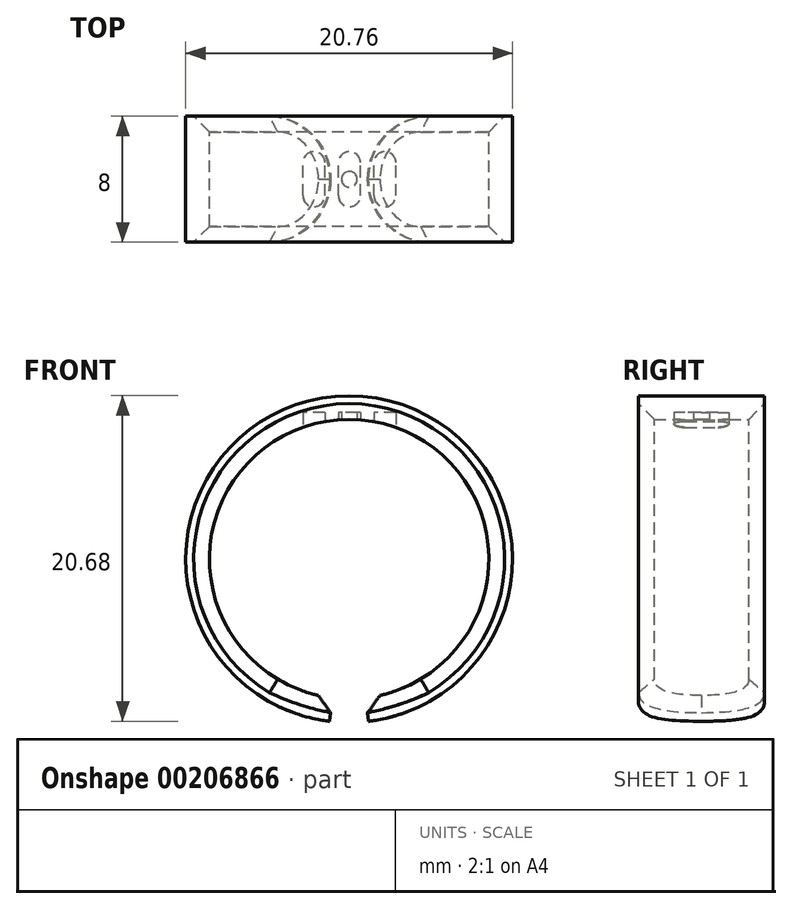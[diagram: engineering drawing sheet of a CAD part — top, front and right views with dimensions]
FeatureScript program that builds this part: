
annotation { "Feature Type Name" : "Feature", "Feature Type Description" : "" }
export const myFeature = defineFeature(function(context is Context, id is Id, definition is map)
    precondition{}
    {
        {
            var Q0;
            Q0=qCreatedBy(makeId("Front.planeOp"),FACE);
            var sketch = newSketch(context, id + "F0", { "sketchPlane" : qUnion([Q0])});
            skCircle(sketch, "E0", {"center": v(0, 0) * mm, "radius": 8.88 * mm});
            skCircle(sketch, "E1.0", {"center": v(0, 0) * mm, "radius": 10.38 * mm});
            skLineSegment(sketch, "E2", {"start": v(0, 0) * mm, "end": v(-1.24, -10.3) * mm});
            skLineSegment(sketch, "E3.MirrorCS", {"start": v(0, 0) * mm, "end": v(1.24, -10.3) * mm});
            skSolve(sketch);
        }
        {
            var Q0;
            {var subQ0=sQuery(id+"F0.wireOp",EDGE,"E2");var subQ1=sQuery(id+"F0.wireOp",EDGE,"E0");var subQ2=makeQuery(id+"F0.imprint","INTERSECT",VERTEX,{"derivedFrom":[subQ1,subQ0]});Q0=makeQuery(id+"F0.imprint","IMPRINT",FACE,{"disambiguationData":[TD([[makeQuery(id+"F0.imprint","IMPRINT",EDGE,{"disambiguationData":[TD([[subQ2,1.0]])],"derivedFrom":subQ1}),-1.0]])]});}
            extrude(context, id + "F1", {"entities" : qUnion([Q0]), "depth" : 4 * mm, "hasSecondDirection" : true, "secondDirectionOppositeDirection" : true, "secondDirectionDepth" : 4 * mm});
        }
        {
            var Q0;
            Q0=makeQuery(id+"F1.opExtrude","CAP_EDGE",EDGE,{"disambiguationData":[OSD([sQuery(id+"F0.wireOp",EDGE,"E3.MirrorCS")])],"isStart":false});
            var Q1;
            Q1=makeQuery(id+"F1.opExtrude","CAP_EDGE",EDGE,{"disambiguationData":[OSD([sQuery(id+"F0.wireOp",EDGE,"E2")])],"isStart":false});
            var Q2;
            Q2=makeQuery(id+"F1.opExtrude","CAP_EDGE",EDGE,{"disambiguationData":[OSD([sQuery(id+"F0.wireOp",EDGE,"E2")])],"isStart":true});
            var Q3;
            Q3=makeQuery(id+"F1.opExtrude","CAP_EDGE",EDGE,{"disambiguationData":[OSD([sQuery(id+"F0.wireOp",EDGE,"E3.MirrorCS")])],"isStart":true});
            fillet(context, id + "F2", {"entities" : qUnion([Q0, Q1, Q2, Q3]), "radius" : 4 * mm, "tangentPropagation" : true, "allowEdgeOverflow" : false});
        }
        {
            var Q0;
            Q0=makeQuery(id+"F1.opExtrude","CAP_EDGE",EDGE,{"disambiguationData":[OSD([sQuery(id+"F0.wireOp",EDGE,"E0")])],"isStart":true});
            var Q1;
            Q1=makeQuery(id+"F1.opExtrude","CAP_EDGE",EDGE,{"disambiguationData":[OSD([sQuery(id+"F0.wireOp",EDGE,"E0")])],"isStart":false});
            var Q2;
            Q2=makeQuery(id+"F2.opFillet","BLEND_EDGE",EDGE,{"blendedFrom":[makeQuery(id+"F1.opExtrude","CAP_EDGE",EDGE,{"disambiguationData":[OSD([sQuery(id+"F0.wireOp",EDGE,"E2")])],"isStart":false}),makeQuery(id+"F1.opExtrude","SWEPT_FACE",FACE,{"disambiguationData":[OSD([sQuery(id+"F0.wireOp",EDGE,"E0")])]})],"blendedInto":[makeQuery(id+"F1.opExtrude","SWEPT_FACE",FACE,{"disambiguationData":[OSD([sQuery(id+"F0.wireOp",EDGE,"E0")])]})]});
            var Q3;
            Q3=makeQuery(id+"F2.opFillet","BLEND_EDGE",EDGE,{"blendedFrom":[makeQuery(id+"F1.opExtrude","CAP_EDGE",EDGE,{"disambiguationData":[OSD([sQuery(id+"F0.wireOp",EDGE,"E3.MirrorCS")])],"isStart":true}),makeQuery(id+"F1.opExtrude","SWEPT_FACE",FACE,{"disambiguationData":[OSD([sQuery(id+"F0.wireOp",EDGE,"E0")])]})],"blendedInto":[makeQuery(id+"F1.opExtrude","SWEPT_FACE",FACE,{"disambiguationData":[OSD([sQuery(id+"F0.wireOp",EDGE,"E0")])]})]});
            chamfer(context, id + "F3", {"entities" : qUnion([Q0, Q1, Q2, Q3]), "width" : 1 * mm, "tangentPropagation" : true});
        }
        {
            var Q0;
            Q0=qCreatedBy(makeId("Top.planeOp"),FACE);
            var sketch = newSketch(context, id + "F4", { "sketchPlane" : qUnion([Q0])});
            skLineSegment(sketch, "E4.bottom", {"start": v(-0.68, 1.05) * mm, "end": v(-0.68, -1.05) * mm});
            skArc(sketch, "E5.filletArc", {"start": v(0.72, 1.05) * mm, "mid": v(0.51, 1.54) * mm, "end": v(0.02, 1.75) * mm});
            skArc(sketch, "E6.filletArc", {"start": v(0.02, 1.75) * mm, "mid": v(-0.48, 1.54) * mm, "end": v(-0.68, 1.05) * mm});
            skArc(sketch, "E7.filletArc", {"start": v(0.02, -1.75) * mm, "mid": v(0.51, -1.54) * mm, "end": v(0.72, -1.05) * mm});
            skArc(sketch, "E8.filletArc", {"start": v(-0.68, -1.05) * mm, "mid": v(-0.48, -1.54) * mm, "end": v(0.02, -1.75) * mm});
            skLineSegment(sketch, "E9.bottom", {"start": v(-2.94, 1.05) * mm, "end": v(-2.94, -1.05) * mm});
            skLineSegment(sketch, "E9.top", {"start": v(-1.54, 1.05) * mm, "end": v(-1.54, -1.05) * mm});
            skArc(sketch, "E10.filletArc", {"start": v(-1.54, 1.05) * mm, "mid": v(-1.74, 1.54) * mm, "end": v(-2.24, 1.75) * mm});
            skArc(sketch, "E11.filletArc", {"start": v(-2.24, 1.75) * mm, "mid": v(-2.73, 1.54) * mm, "end": v(-2.94, 1.05) * mm});
            skArc(sketch, "E12.filletArc", {"start": v(-2.24, -1.75) * mm, "mid": v(-1.74, -1.54) * mm, "end": v(-1.54, -1.05) * mm});
            skArc(sketch, "E13.filletArc", {"start": v(-2.94, -1.05) * mm, "mid": v(-2.73, -1.54) * mm, "end": v(-2.24, -1.75) * mm});
            skLineSegment(sketch, "E14", {"start": v(0.72, 1.05) * mm, "end": v(0.72, -1.05) * mm});
            skCircle(sketch, "E15", {"center": v(0.01, 0) * mm, "radius": 0.5 * mm});
            skLineSegment(sketch, "E16.bottom", {"start": v(1.57, 1.05) * mm, "end": v(1.57, -1.05) * mm});
            skLineSegment(sketch, "E16.top", {"start": v(2.97, 1.05) * mm, "end": v(2.97, -1.05) * mm});
            skArc(sketch, "E17.filletArc", {"start": v(2.97, 1.05) * mm, "mid": v(2.76, 1.54) * mm, "end": v(2.27, 1.75) * mm});
            skArc(sketch, "E18.filletArc", {"start": v(2.27, 1.75) * mm, "mid": v(1.77, 1.54) * mm, "end": v(1.57, 1.05) * mm});
            skArc(sketch, "E19.filletArc", {"start": v(2.27, -1.75) * mm, "mid": v(2.76, -1.54) * mm, "end": v(2.97, -1.05) * mm});
            skArc(sketch, "E20.filletArc", {"start": v(1.57, -1.05) * mm, "mid": v(1.77, -1.54) * mm, "end": v(2.27, -1.75) * mm});
            skSolve(sketch);
        }
        {
            var Q0;
            Q0=makeQuery(id+"F4.imprint","IMPRINT",FACE,{"disambiguationData":[TD([[makeQuery(id+"F4.imprint","IMPRINT",EDGE,{"derivedFrom":sQuery(id+"F4.wireOp",EDGE,"E16.bottom")}),1.0]])]});
            var Q1;
            Q1=makeQuery(id+"F4.imprint","IMPRINT",FACE,{"disambiguationData":[TD([[makeQuery(id+"F4.imprint","IMPRINT",EDGE,{"derivedFrom":sQuery(id+"F4.wireOp",EDGE,"E4.bottom")}),1.0]])]});
            var Q2;
            Q2=makeQuery(id+"F4.imprint","IMPRINT",FACE,{"disambiguationData":[TD([[makeQuery(id+"F4.imprint","IMPRINT",EDGE,{"derivedFrom":sQuery(id+"F4.wireOp",EDGE,"E9.bottom")}),1.0]])]});
            extrude(context, id + "F5", {"entities" : qUnion([Q0, Q1, Q2]), "operationType" : NewBodyOperationType.REMOVE, "depth" : 9.3 * mm});
        }
    });
